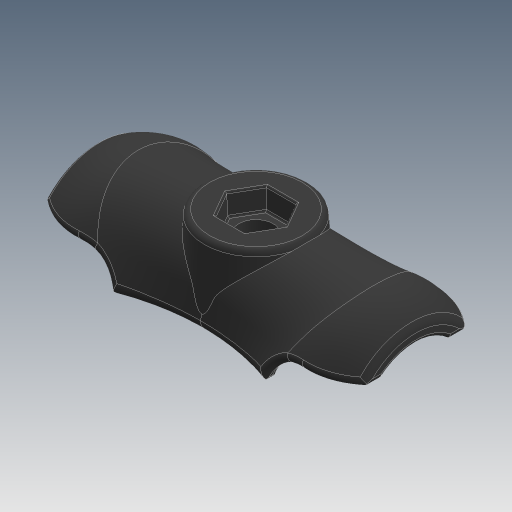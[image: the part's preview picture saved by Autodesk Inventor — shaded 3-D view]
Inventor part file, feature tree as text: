
AUTODESK INVENTOR PART (.ipt)
format: ipt  version: 2023.1 (Build 271208000, 208)  size: 1,019,904 bytes
history: native  units: mm
features: sketch x9, extrude x5, other x4, fillet x4, loft x1, revolve x1
ambient origin geometry x8: Origin, YZ Plane, XZ Plane, XY Plane, X Axis, Y Axis, Z Axis, Center Point
bodies: Solido1 (feature_tree)
feature tree (24):
  sketch  "Schizzo5"
  other  "Piano di lavoro1"
  sketch  "Schizzo6"
  sketch  "Schizzo7"
  other  "Piano di lavoro2"
  sketch  "Schizzo8"
  sketch  "Schizzo9"
  other  "Piano di lavoro4"
  loft  "Loft1"
  other  "Piano di lavoro5"
  extrude  "Estrusione1"  Depth=90.424mm
  sketch  "Schizzo12"
  extrude  "Estrusione2"  Depth=2.794mm
  extrude  "Estrusione3"  Depth=25.146mm
  extrude  "Estrusione5"  Depth=19.05mm
  fillet  "Raccordo1"  Radius=4.0mm
  fillet  "Raccordo2"  Radius=31.9mm
  extrude  "Estrusione4"  Depth=23.05mm
  revolve  "Rivoluzione1"
  fillet  "Raccordo12"  Radius=23.05mm
  fillet  "Raccordo13"  Radius=15.0mm
  sketch  "Schizzo11"
  sketch  "Schizzo13"
  sketch  "Schizzo14"
